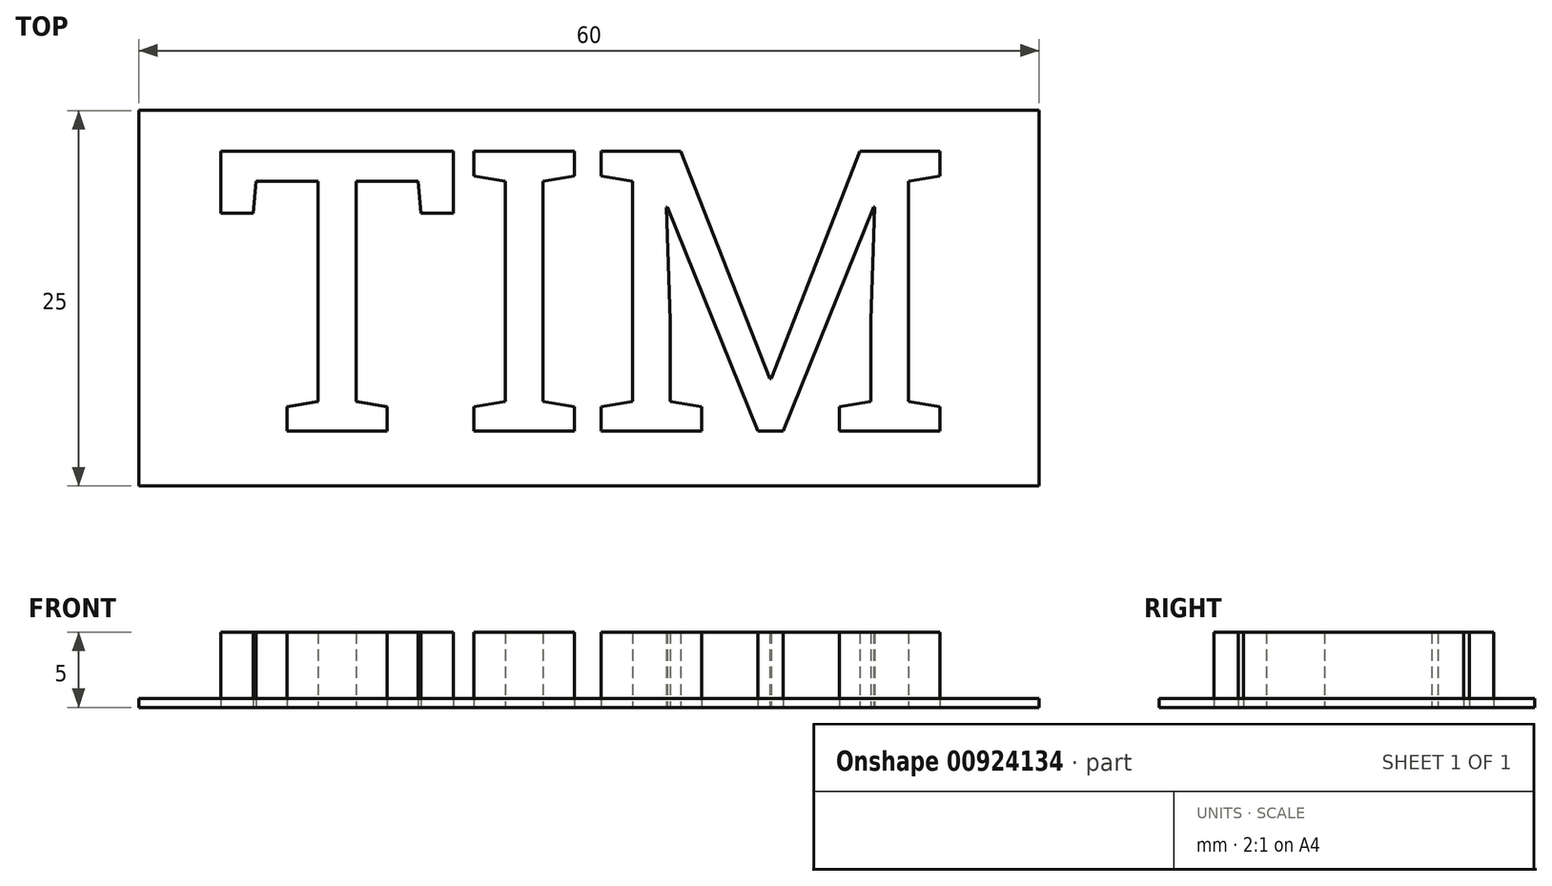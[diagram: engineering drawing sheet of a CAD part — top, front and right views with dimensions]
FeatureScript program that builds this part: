
annotation { "Feature Type Name" : "Feature", "Feature Type Description" : "" }
export const myFeature = defineFeature(function(context is Context, id is Id, definition is map)
    precondition{}
    {
        {
            var Q0;
            Q0=qCreatedBy(makeId("Top.planeOp"),FACE);
            var sketch = newSketch(context, id + "F0", { "sketchPlane" : qUnion([Q0])});
            skLineSegment(sketch, "E0.bottom", {"start": v(-21.45, 9.11) * mm, "end": v(38.55, 9.11) * mm});
            skLineSegment(sketch, "E0.top", {"start": v(-21.45, -15.89) * mm, "end": v(38.55, -15.89) * mm});
            skLineSegment(sketch, "E0.left", {"start": v(-21.45, 9.11) * mm, "end": v(-21.45, -15.89) * mm});
            skLineSegment(sketch, "E0.right", {"start": v(38.55, 9.11) * mm, "end": v(38.55, -15.89) * mm});
            skText(sketch, "E1", { "text": "TIM", "fontName": "RobotoSlab-Regular.ttf"});
            const initialGuessF0  = {"E1": [-0.01645, -0.01225, 1, 0, 0.01887]};
            skSetInitialGuess(sketch, initialGuessF0);
            skSolve(sketch);
        }
        {
            var Q0;
            Q0=makeQuery(id+"F0.imprint","IMPRINT",FACE,{"disambiguationData":[TD([[makeQuery(id+"F0.imprint","IMPRINT",EDGE,{"derivedFrom":sQuery(id+"F0.wireOp",EDGE,"E1.sketch_text.stroke-0")}),-1.0]])]});
            var Q1;
            Q1=makeQuery(id+"F0.imprint","IMPRINT",FACE,{"disambiguationData":[TD([[makeQuery(id+"F0.imprint","IMPRINT",EDGE,{"derivedFrom":sQuery(id+"F0.wireOp",EDGE,"E0.bottom")}),-1.0]])]});
            var Q2;
            Q2=makeQuery(id+"F0.imprint","IMPRINT",FACE,{"disambiguationData":[TD([[makeQuery(id+"F0.imprint","IMPRINT",EDGE,{"derivedFrom":sQuery(id+"F0.wireOp",EDGE,"E1.sketch_text.stroke-16")}),-1.0]])]});
            var Q3;
            Q3=makeQuery(id+"F0.imprint","IMPRINT",FACE,{"disambiguationData":[TD([[makeQuery(id+"F0.imprint","IMPRINT",EDGE,{"derivedFrom":sQuery(id+"F0.wireOp",EDGE,"E1.sketch_text.stroke-28")}),-1.0]])]});
            extrude(context, id + "F1", {"entities" : qUnion([Q0, Q1, Q2, Q3]), "depth" : .6 * mm, "offsetDistance" : 25 * mm});
        }
        {
            var Q0;
            Q0=makeQuery(id+"F0.imprint","IMPRINT",FACE,{"disambiguationData":[TD([[makeQuery(id+"F0.imprint","IMPRINT",EDGE,{"derivedFrom":sQuery(id+"F0.wireOp",EDGE,"E1.sketch_text.stroke-0")}),-1.0]])]});
            var Q1;
            Q1=makeQuery(id+"F0.imprint","IMPRINT",FACE,{"disambiguationData":[TD([[makeQuery(id+"F0.imprint","IMPRINT",EDGE,{"derivedFrom":sQuery(id+"F0.wireOp",EDGE,"E1.sketch_text.stroke-16")}),-1.0]])]});
            var Q2;
            Q2=makeQuery(id+"F0.imprint","IMPRINT",FACE,{"disambiguationData":[TD([[makeQuery(id+"F0.imprint","IMPRINT",EDGE,{"derivedFrom":sQuery(id+"F0.wireOp",EDGE,"E1.sketch_text.stroke-28")}),-1.0]])]});
            extrude(context, id + "F2", {"entities" : qUnion([Q0, Q1, Q2]), "depth" : 5 * mm, "offsetDistance" : 25 * mm});
        }
    });
